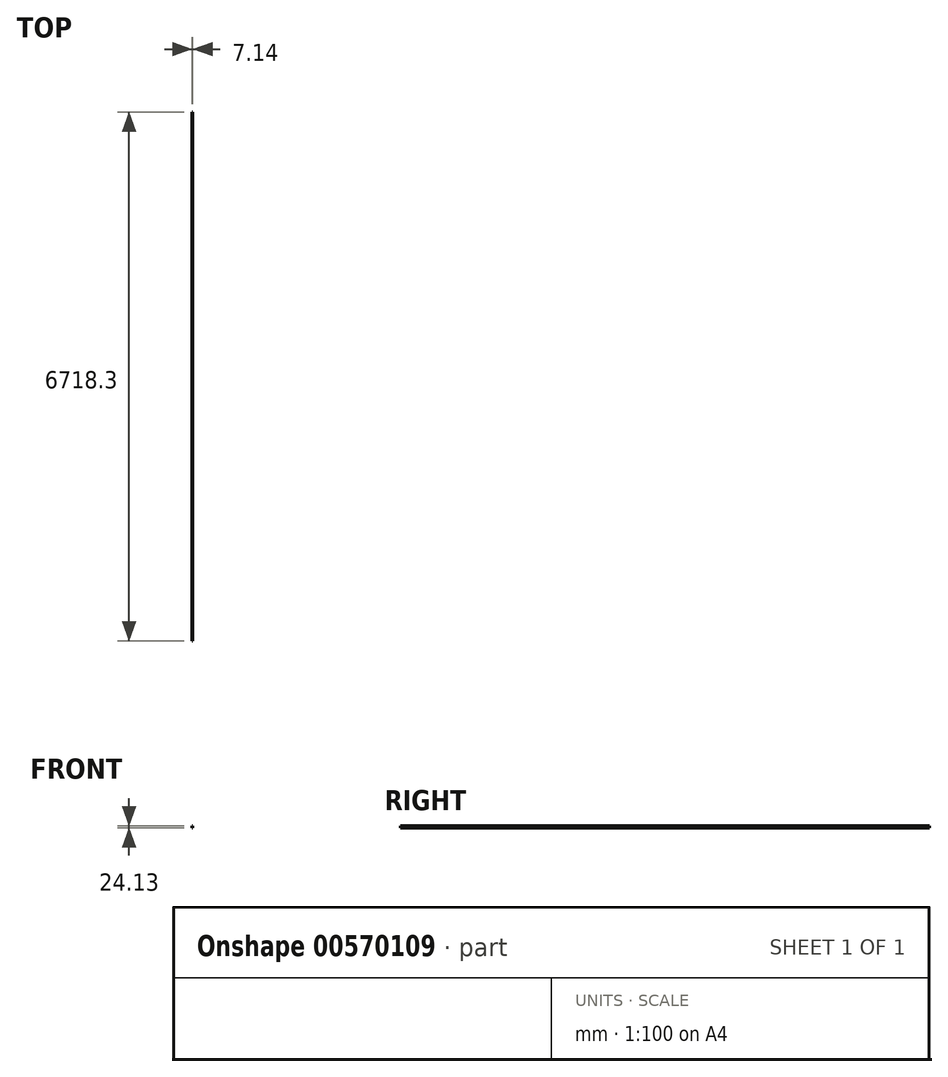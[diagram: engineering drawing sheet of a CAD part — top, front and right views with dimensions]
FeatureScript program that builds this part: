
annotation { "Feature Type Name" : "Feature", "Feature Type Description" : "" }
export const myFeature = defineFeature(function(context is Context, id is Id, definition is map)
    precondition{}
    {
        {
            var Q0;
            Q0=qCreatedBy(makeId("Front.planeOp"),FACE);
            var sketch = newSketch(context, id + "F0", { "sketchPlane" : qUnion([Q0])});
            skLineSegment(sketch, "E0.bottom", {"start": v(0, 0) * mm, "end": v(7.14, 0) * mm});
            skLineSegment(sketch, "E0.top", {"start": v(0, -24.13) * mm, "end": v(7.14, -24.13) * mm});
            skLineSegment(sketch, "E0.left", {"start": v(0, 0) * mm, "end": v(0, -24.13) * mm});
            skLineSegment(sketch, "E0.right", {"start": v(7.14, 0) * mm, "end": v(7.14, -24.13) * mm});
            skSolve(sketch);
        }
        {
            var Q0;
            Q0=makeQuery(id+"F0.imprint","IMPRINT",FACE,{"disambiguationData":[TD([[makeQuery(id+"F0.imprint","IMPRINT",EDGE,{"derivedFrom":sQuery(id+"F0.wireOp",EDGE,"E0.bottom")}),-1.0]])]});
            extrude(context, id + "F1", {"entities" : qUnion([Q0]), "depth" : 6718.3 * mm, "offsetDistance" : 25.4 * mm});
        }
    });
